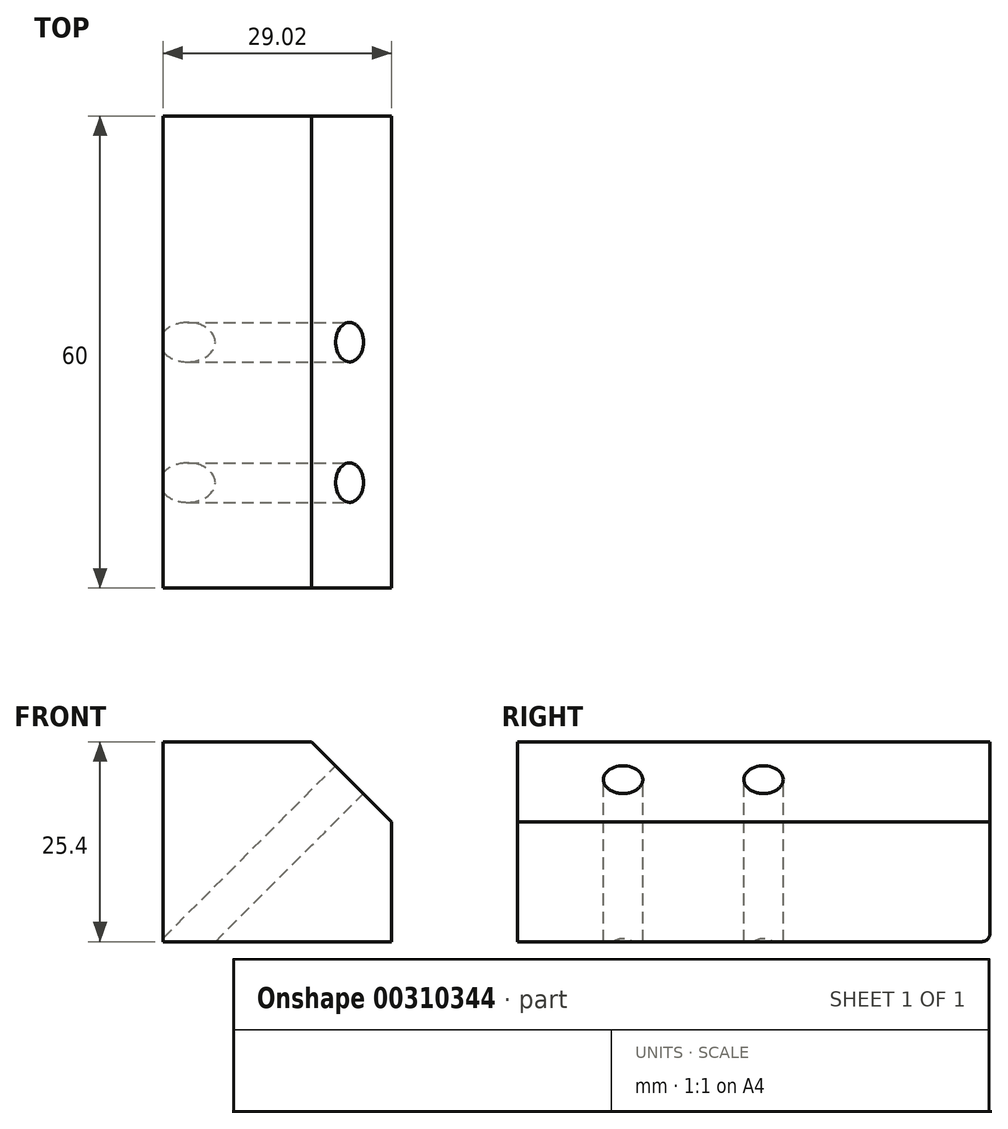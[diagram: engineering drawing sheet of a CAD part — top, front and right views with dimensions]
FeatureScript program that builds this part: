
annotation { "Feature Type Name" : "Feature", "Feature Type Description" : "" }
export const myFeature = defineFeature(function(context is Context, id is Id, definition is map)
    precondition{}
    {
        {
            var Q0;
            Q0=qCreatedBy(makeId("Top.planeOp"),FACE);
            var sketch = newSketch(context, id + "F0", { "sketchPlane" : qUnion([Q0])});
            skLineSegment(sketch, "E0.bottom", {"start": v(0, 0) * mm, "end": v(-29.02, 0) * mm});
            skLineSegment(sketch, "E0.top", {"start": v(0, 60) * mm, "end": v(-29.02, 60) * mm});
            skLineSegment(sketch, "E0.left", {"start": v(0, 0) * mm, "end": v(0, 60) * mm});
            skLineSegment(sketch, "E0.right", {"start": v(-29.02, 0) * mm, "end": v(-29.02, 60) * mm});
            skSolve(sketch);
        }
        {
            var Q0;
            Q0=makeQuery(id+"F0.imprint","IMPRINT",FACE,{"disambiguationData":[TD([[makeQuery(id+"F0.imprint","IMPRINT",EDGE,{"derivedFrom":sQuery(id+"F0.wireOp",EDGE,"E0.bottom")}),-1.0]])]});
            extrude(context, id + "F1", {"entities" : qUnion([Q0]), "depth" : 25.4 * mm});
        }
        {
            var Q0;
            Q0=makeQuery(id+"F1.opExtrude","CAP_EDGE",EDGE,{"disambiguationData":[OSD([sQuery(id+"F0.wireOp",EDGE,"E0.left")])],"isStart":false});
            chamfer(context, id + "F2", {"entities" : qUnion([Q0]), "width" : 10.16 * mm, "tangentPropagation" : true});
        }
        {
            var Q0;
            Q0=makeQuery(id+"F2.opChamfer","BLEND_FACE",FACE,{"disambiguationData":[OSD([sQuery(id+"F0.wireOp",EDGE,"E0.left")])]});
            var sketch = newSketch(context, id + "F3", { "sketchPlane" : qUnion([Q0])});
            skPoint(sketch, "E1", {"position": v(13.41, 18.33) * mm});
            skPoint(sketch, "E2", {"position": v(31.25, 18.33) * mm});
            skSolve(sketch);
        }
        {
            var Q0;
            Q0=sQuery(id+"F3.wireOp",VERTEX,"E1");
            var Q1;
            Q1=sQuery(id+"F3.wireOp",VERTEX,"E2");
            var Q2;
            Q2=makeQuery(id+"F1.opExtrude","SWEPT_BODY",BODY,{"disambiguationData":[OSD([sQuery(id+"F0.wireOp",EDGE,"E0.bottom"),sQuery(id+"F0.wireOp",EDGE,"E0.top"),sQuery(id+"F0.wireOp",EDGE,"E0.left"),sQuery(id+"F0.wireOp",EDGE,"E0.right")])]});
            hole(context, id + "F4", {"style" : HoleStyle.SIMPLE, "endStyle" : HoleEndStyle.THROUGH, "standardTappedOrClearance" : lookupTablePath({ "standard" : "ISO", "engagement" : "75%", "pitch" : "1 mm", "size" : "M6", "type" : "Tapped" }), "standardBlindInLast" : lookupTablePath({ "standard" : "ISO", "engagement" : "75%", "pitch" : "1 mm", "size" : "M6", "type" : "Tapped" }), "holeDiameter" : 5 * mm, "showTappedDepth" : true, "tappedDepth" : 12.7 * mm, "tapClearance" : 3, "locations" : qUnion([Q0, Q1]), "scope" : qUnion([Q2]), "majorDiameter" : 6 * mm});
        }
        {
            var Q0;
            Q0=makeQuery(id+"F1.opExtrude","CAP_EDGE",EDGE,{"disambiguationData":[OSD([sQuery(id+"F0.wireOp",EDGE,"E0.top")])],"isStart":true});
            fillet(context, id + "F5", {"entities" : qUnion([Q0]), "radius" : 1 * mm, "tangentPropagation" : true, "allowEdgeOverflow" : false});
        }
    });
